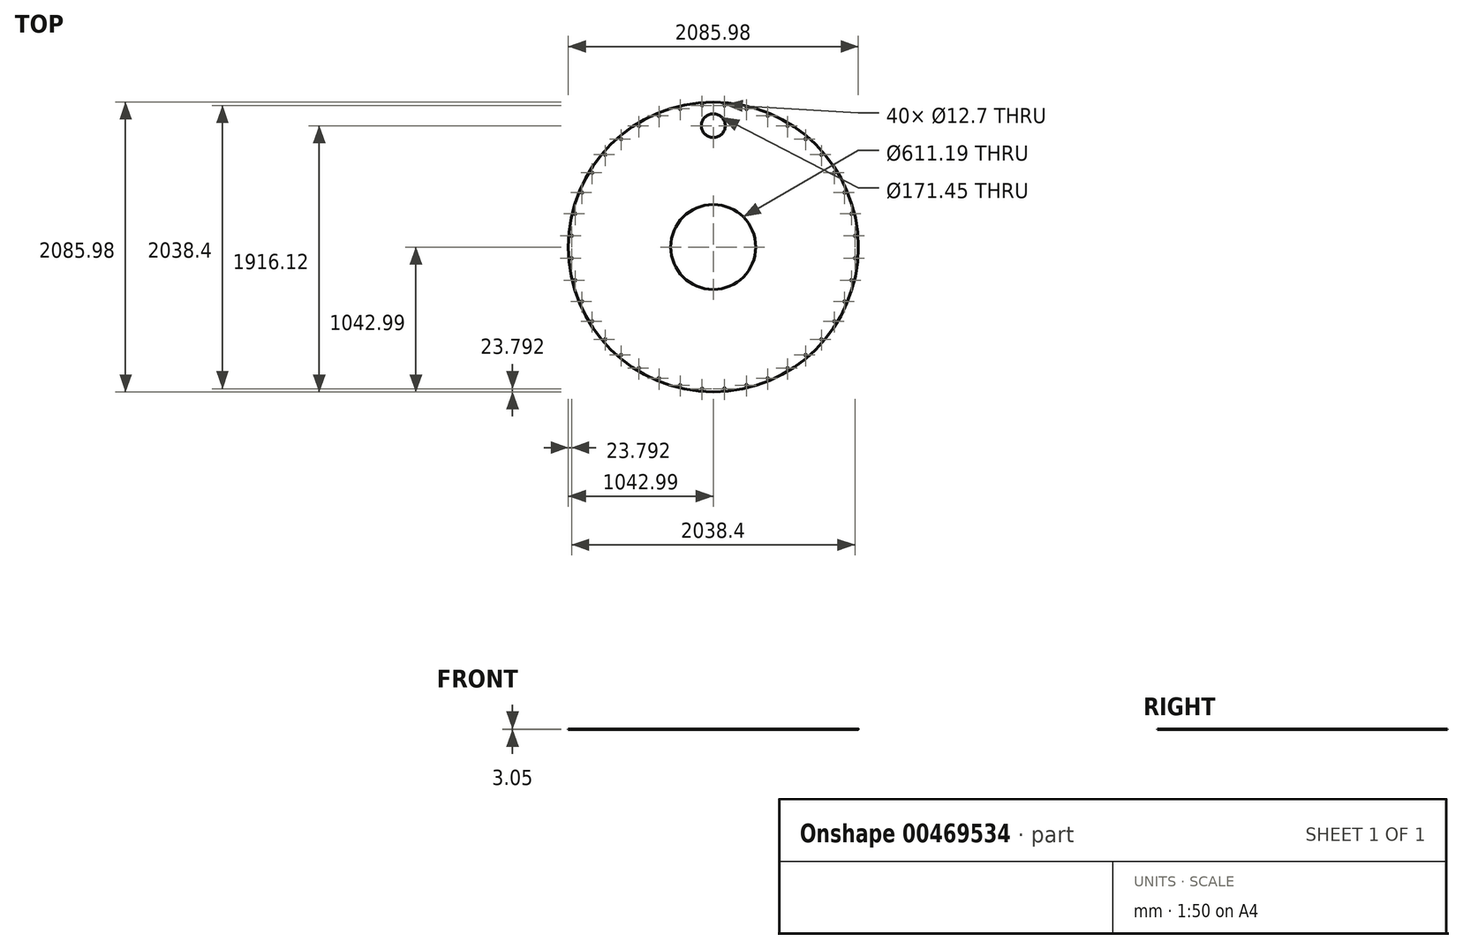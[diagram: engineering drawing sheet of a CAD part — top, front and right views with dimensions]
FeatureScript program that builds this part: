
annotation { "Feature Type Name" : "Feature", "Feature Type Description" : "" }
export const myFeature = defineFeature(function(context is Context, id is Id, definition is map)
    precondition{}
    {
        {
            var Q0;
            Q0=qCreatedBy(makeId("Top.planeOp"),FACE);
            var sketch = newSketch(context, id + "F0", { "sketchPlane" : qUnion([Q0])});
            skCircle(sketch, "E0", {"center": v(0, 0) * mm, "radius": 1042.99 * mm});
            skCircle(sketch, "E1", {"center": v(0, 0) * mm, "radius": 305.6 * mm});
            skCircle(sketch, "E2", {"center": v(0, 873.13) * mm, "radius": 85.73 * mm});
            skCircle(sketch, "E3", {"center": v(0, 0) * mm, "radius": 1022.35 * mm, "construction": true});
            skCircle(sketch, "E4", {"center": v(1019.2, 80.21) * mm, "radius": 6.35 * mm});
            skLineSegment(sketch, "E5", {"start": v(1019.2, 80.21) * mm, "end": v(0, 0) * mm, "construction": true});
            skCircle(sketch, "E6.1.0", {"center": v(994.1, 238.66) * mm, "radius": 6.35 * mm});
            skCircle(sketch, "E6.2.0", {"center": v(944.53, 391.24) * mm, "radius": 6.35 * mm});
            skCircle(sketch, "E6.3.0", {"center": v(871.7, 534.18) * mm, "radius": 6.35 * mm});
            skCircle(sketch, "E6.4.0", {"center": v(777.4, 663.96) * mm, "radius": 6.35 * mm});
            skCircle(sketch, "E6.5.0", {"center": v(663.96, 777.4) * mm, "radius": 6.35 * mm});
            skCircle(sketch, "E6.6.0", {"center": v(534.18, 871.7) * mm, "radius": 6.35 * mm});
            skCircle(sketch, "E6.7.0", {"center": v(391.24, 944.53) * mm, "radius": 6.35 * mm});
            skCircle(sketch, "E6.8.0", {"center": v(238.66, 994.1) * mm, "radius": 6.35 * mm});
            skCircle(sketch, "E6.9.0", {"center": v(80.21, 1019.2) * mm, "radius": 6.35 * mm});
            skCircle(sketch, "E6.10.0", {"center": v(-80.21, 1019.2) * mm, "radius": 6.35 * mm});
            skCircle(sketch, "E6.11.0", {"center": v(-238.66, 994.1) * mm, "radius": 6.35 * mm});
            skCircle(sketch, "E6.12.0", {"center": v(-391.24, 944.53) * mm, "radius": 6.35 * mm});
            skCircle(sketch, "E6.13.0", {"center": v(-534.18, 871.7) * mm, "radius": 6.35 * mm});
            skCircle(sketch, "E6.14.0", {"center": v(-663.96, 777.4) * mm, "radius": 6.35 * mm});
            skCircle(sketch, "E6.15.0", {"center": v(-777.4, 663.96) * mm, "radius": 6.35 * mm});
            skCircle(sketch, "E6.16.0", {"center": v(-871.7, 534.18) * mm, "radius": 6.35 * mm});
            skCircle(sketch, "E6.17.0", {"center": v(-944.53, 391.24) * mm, "radius": 6.35 * mm});
            skCircle(sketch, "E6.18.0", {"center": v(-994.1, 238.66) * mm, "radius": 6.35 * mm});
            skCircle(sketch, "E6.19.0", {"center": v(-1019.2, 80.21) * mm, "radius": 6.35 * mm});
            skCircle(sketch, "E6.20.0", {"center": v(-1019.2, -80.21) * mm, "radius": 6.35 * mm});
            skCircle(sketch, "E6.21.0", {"center": v(-994.1, -238.66) * mm, "radius": 6.35 * mm});
            skCircle(sketch, "E6.22.0", {"center": v(-944.53, -391.24) * mm, "radius": 6.35 * mm});
            skCircle(sketch, "E6.23.0", {"center": v(-871.7, -534.18) * mm, "radius": 6.35 * mm});
            skCircle(sketch, "E6.24.0", {"center": v(-777.4, -663.96) * mm, "radius": 6.35 * mm});
            skCircle(sketch, "E6.25.0", {"center": v(-663.96, -777.4) * mm, "radius": 6.35 * mm});
            skCircle(sketch, "E6.26.0", {"center": v(-534.18, -871.7) * mm, "radius": 6.35 * mm});
            skCircle(sketch, "E6.27.0", {"center": v(-391.24, -944.53) * mm, "radius": 6.35 * mm});
            skCircle(sketch, "E6.28.0", {"center": v(-238.66, -994.1) * mm, "radius": 6.35 * mm});
            skCircle(sketch, "E6.29.0", {"center": v(-80.21, -1019.2) * mm, "radius": 6.35 * mm});
            skCircle(sketch, "E6.30.0", {"center": v(80.21, -1019.2) * mm, "radius": 6.35 * mm});
            skCircle(sketch, "E6.31.0", {"center": v(238.66, -994.1) * mm, "radius": 6.35 * mm});
            skCircle(sketch, "E6.32.0", {"center": v(391.24, -944.53) * mm, "radius": 6.35 * mm});
            skCircle(sketch, "E6.33.0", {"center": v(534.18, -871.7) * mm, "radius": 6.35 * mm});
            skCircle(sketch, "E6.34.0", {"center": v(663.96, -777.4) * mm, "radius": 6.35 * mm});
            skCircle(sketch, "E6.35.0", {"center": v(777.4, -663.96) * mm, "radius": 6.35 * mm});
            skCircle(sketch, "E6.36.0", {"center": v(871.7, -534.18) * mm, "radius": 6.35 * mm});
            skCircle(sketch, "E6.37.0", {"center": v(944.53, -391.24) * mm, "radius": 6.35 * mm});
            skCircle(sketch, "E6.38.0", {"center": v(994.1, -238.66) * mm, "radius": 6.35 * mm});
            skCircle(sketch, "E6.39.0", {"center": v(1019.2, -80.21) * mm, "radius": 6.35 * mm});
            skLineSegment(sketch, "E7", {"start": v(0, 0) * mm, "end": v(1019.2, -80.21) * mm, "construction": true});
            skSolve(sketch);
        }
        {
            var Q0;
            Q0 = qSketchRegion(id + "F0", true);
            extrude(context, id + "F1", {"entities" : qUnion([Q0]), "depth" : 3.05 * mm, "offsetDistance" : 25.4 * mm});
        }
    });
